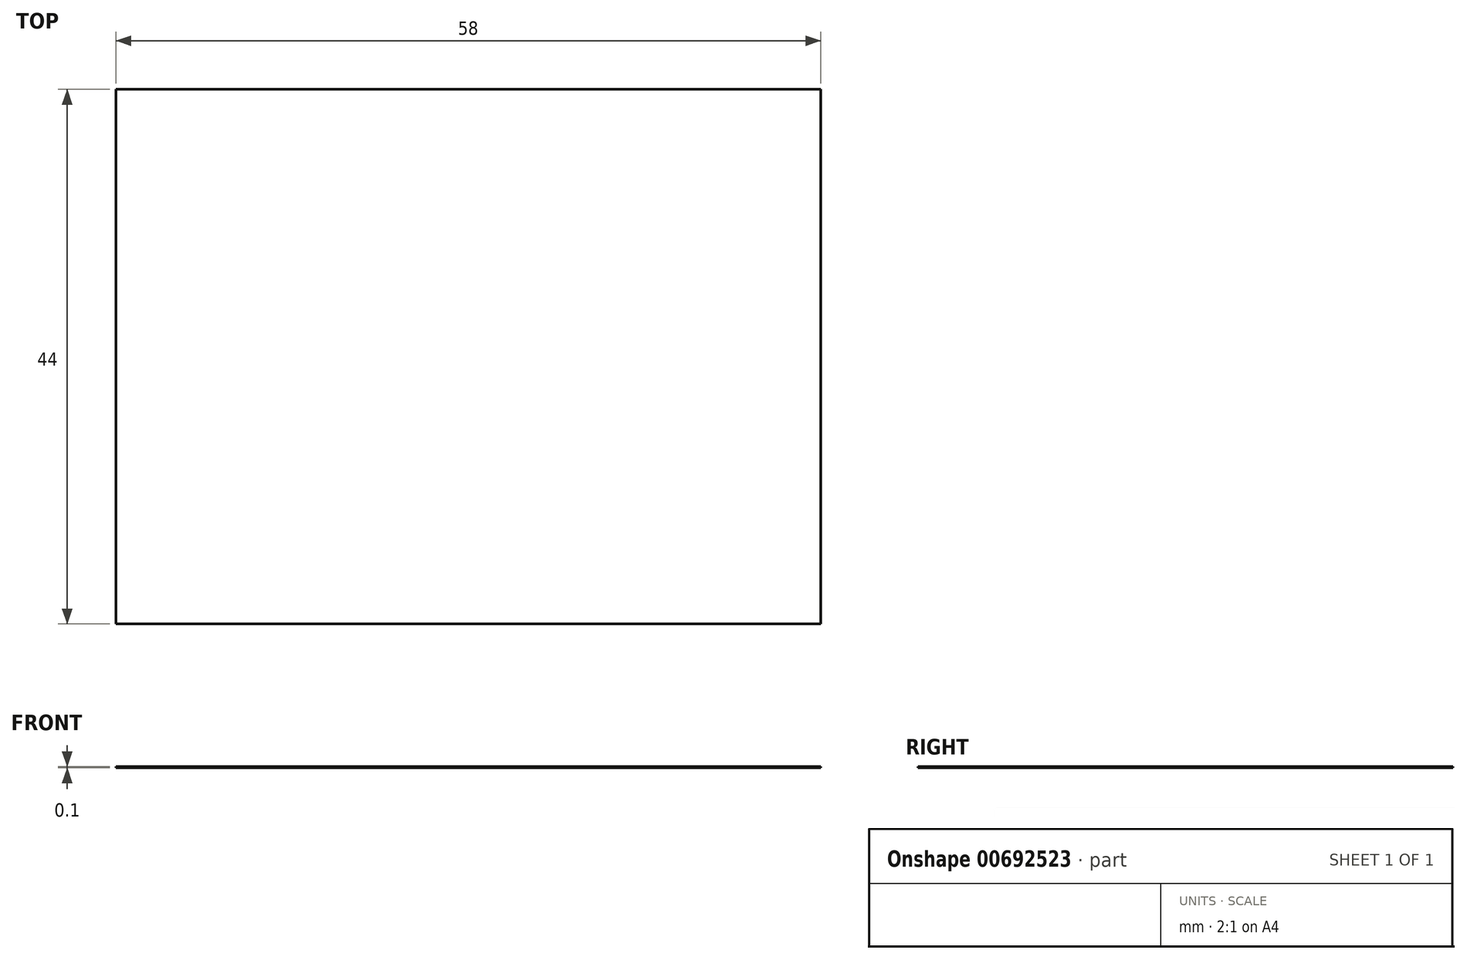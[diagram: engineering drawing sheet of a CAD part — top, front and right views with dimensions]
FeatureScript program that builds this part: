
annotation { "Feature Type Name" : "Feature", "Feature Type Description" : "" }
export const myFeature = defineFeature(function(context is Context, id is Id, definition is map)
    precondition{}
    {
        {
            var Q0;
            Q0=qCreatedBy(makeId("Top.planeOp"),FACE);
            var sketch = newSketch(context, id + "F0", { "sketchPlane" : qUnion([Q0])});
            skLineSegment(sketch, "E0.bottom", {"start": v(29, 22) * mm, "end": v(-29, 22) * mm});
            skLineSegment(sketch, "E0.top", {"start": v(29, -22) * mm, "end": v(-29, -22) * mm});
            skLineSegment(sketch, "E0.left", {"start": v(29, 22) * mm, "end": v(29, -22) * mm});
            skLineSegment(sketch, "E0.right", {"start": v(-29, 22) * mm, "end": v(-29, -22) * mm});
            skPoint(sketch, "E0.middle", {"position": v(0, 0) * mm});
            skSolve(sketch);
        }
        {
            var Q0;
            Q0 = qSketchRegion(id + "F0", true);
            extrude(context, id + "F1", {"entities" : qUnion([Q0]), "depth" : 0.1 * mm, "offsetDistance" : 25 * mm});
        }
    });
